# Revit family: NTO_Stng_PippinLoungeChair-PIP10
name_source: partatom
category: Furniture
units: mm (PartAtom-declared; Revit-internal decimal feet)

## family parameters
Always vertical = Yes
Cut with Voids When Loaded = No
Enable Cutting in Views = No
Render Appearance Source = Family Geometry
Room Calculation Point = No
Shared = Yes
Work Plane-Based = No

## types (4) — shared parameters
AssetType = Movable
BIMObjectName = NTO_Pippin_LoungeChair
Category = Pr_40_50_12_48 : Lounge Chairs
ChairFabric = NTO_Textile_Beige
Color = Offwhite Upholstery
DurationUnit = year
ExpectedLife = 10
Features = Textile available in any of NaughtOne standard offering or COM
Finish = Textile
IfcExportAs = IfcFurnitureType
IfcExportType = Chair
MainColor = Offwhite Upholstery
Manufacturer = NaughtOne
ManufacturerName = NaughtOne
ManufacturerURL = www.naughtone.com
Material = Textile available in any of NaughtOne standard offering or COM
Model = Pippin Lounge Chair
NBSDescription = Chair
NBSReference = 45-35-72/352
Name = Pippin Lounge Chair
ProductInformation = www.naughtone.com/products/pippin
Size = 530 x 760 x 760 mm
530 x 760 x 760 mm
URL = www.naughtone.com
Uniclass2015Code = Pr_40_50_12_48
Uniclass2015Title = Lounge Chairs
Uniclass2015Version = Products v1.30
Version = 1
WarrantyDescription = 10 Years
WarrantyDurationUnit = year
zero-valued in all types: Default Elevation

## per-type parameters (varying)
| type | Description | HandleMaterial | HasHandle | Keynote | ModelNumber | ModelReference | RollerFeet | StandardFeet |
| NTO_PippingLoungeChairGlides_PIP10GLN | Pippin Lounge Chair - Glides | NTO_Handle_Blue | No | NOPIP10GLN
NOPIP10GLN | NOPIP10GLN
NOPIP10GLN | Pippin Lounge Chair - Glides | No | Yes |
| NTO_PippingLoungeChairCastorsAndStrapHandle_NOPIP10CSH | Pippin Lounge Chair - Castors and Strap Handle | NTO_Handle_Blue | Yes | NOPIP10CSH | NOPIP10CSH | Pippin Lounge Chair - Castors and Strap Handle | Yes | No |
| NTO_PippingLoungeChairCastors_NOPIP10CSN | Pippin Lounge Chair - Castors | NTO_Handle_Orange | No | NOPIP10CSN | NOPIP10CSN | Pippin Lounge Chair - Castors | Yes | No |
| NTO_PippingLoungeChairGlidesAndStrapHandle_PIP10GLH | Pipping Lounge Chair - Glides and Strap Handle | NTO_Handle_Orange | Yes | NOPIP10GLH | NOPIP10GLH | Pipping Lounge Chair - Glides and Strap Handle | No | Yes |

## geometry (parser evidence)
native form markers: Sweep x12
no freeform markers — native parametric forms only
